# Revit family: ASL_Plus_Series_Floor_Track_90mm_Stud
name_source: partatom
category: Detail Items
revit_build: Autodesk Revit 2018 (Build: 20170223_1515(x64)
units: mm (PartAtom-declared; Revit-internal decimal feet)

## family parameters
Rotate with component = No
Section Shape = Not Defined
Shared = Yes

## types (2) — shared parameters
Manufacturer = Aluminate Solutions Limited
Technical Info = www.aluminate.nz
Type Comments = Plus Series

## per-type parameters (varying)
| type | Floor Track_ASL_747 | Floor Track_ASL_753 | Plastboard Movement | Plasterboard Depth |
| 80mm Negative Floor Track 90mm Stud 13mm Gib BS | No | Yes | 48 mm  [stored 0.15748 ft] | 114 mm  [stored 0.374016 ft] |
| 40mm Negative Floor Track 90mm Stud 13mm Gib BS | Yes | No | 47 mm | 75 mm |

note: [stored X ft] marks values corroborated as IEEE doubles in the binary element streams (Revit-internal decimal feet)

## geometry (parser evidence)
native form markers: Sweep x3
no freeform markers — native parametric forms only
